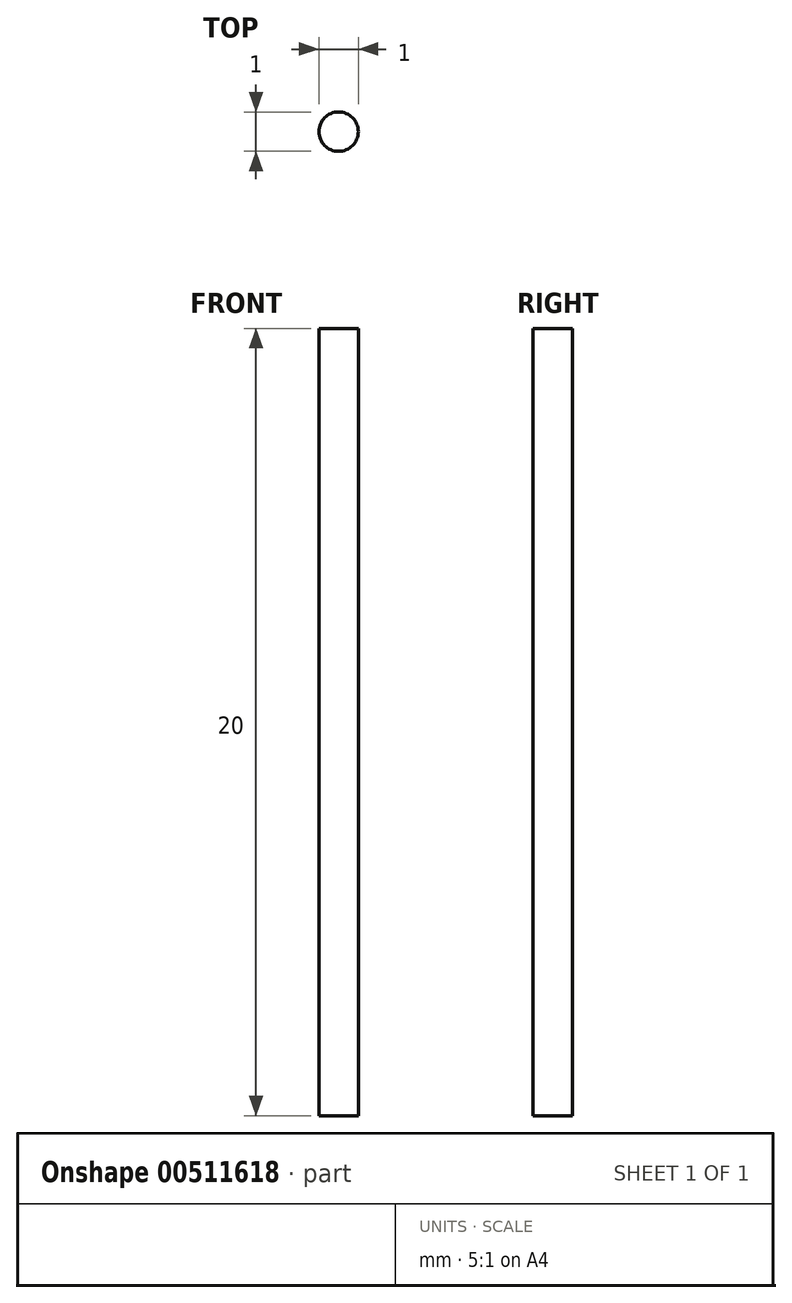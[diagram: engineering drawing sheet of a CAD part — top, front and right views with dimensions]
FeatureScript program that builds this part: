
annotation { "Feature Type Name" : "Feature", "Feature Type Description" : "" }
export const myFeature = defineFeature(function(context is Context, id is Id, definition is map)
    precondition{}
    {
        {
            var Q0;
            Q0=qCreatedBy(makeId("Top.planeOp"),FACE);
            var sketch = newSketch(context, id + "F0", { "sketchPlane" : qUnion([Q0])});
            skCircle(sketch, "E0", {"center": v(0, 0) * mm, "radius": 1.5 * mm});
            skCircle(sketch, "E1", {"center": v(0, 0) * mm, "radius": 0.5 * mm});
            skCircle(sketch, "E2", {"center": v(0, 0) * mm, "radius": 1 * mm});
            skSolve(sketch);
        }
        {
            var Q0;
            Q0=makeQuery(id+"F0.imprint","IMPRINT",FACE,{"disambiguationData":[TD([[makeQuery(id+"F0.imprint","IMPRINT",EDGE,{"derivedFrom":sQuery(id+"F0.wireOp",EDGE,"P2dCeyrW-3yyO-GLKp-AFtS-Teg8QAAx5zQA")}),1.0]])]});
            var Q1;
            Q1=makeQuery(id+"F0.imprint","IMPRINT",FACE,{"disambiguationData":[TD([[makeQuery(id+"F0.imprint","IMPRINT",EDGE,{"derivedFrom":sQuery(id+"F0.wireOp",EDGE,"eUsNJooS-I5Mt-Ymv3-55p3-Y8ifr9MI58IP")}),1.0]])]});
            var Q2;
            Q2=makeQuery(id+"F0.imprint","IMPRINT",FACE,{"disambiguationData":[TD([[makeQuery(id+"F0.imprint","IMPRINT",EDGE,{"derivedFrom":sQuery(id+"F0.wireOp",EDGE,"E1")}),1.0]])]});
            extrude(context, id + "F1", {"entities" : qUnion([Q0, Q1, Q2]), "depth" : 20 * mm});
        }
    });
